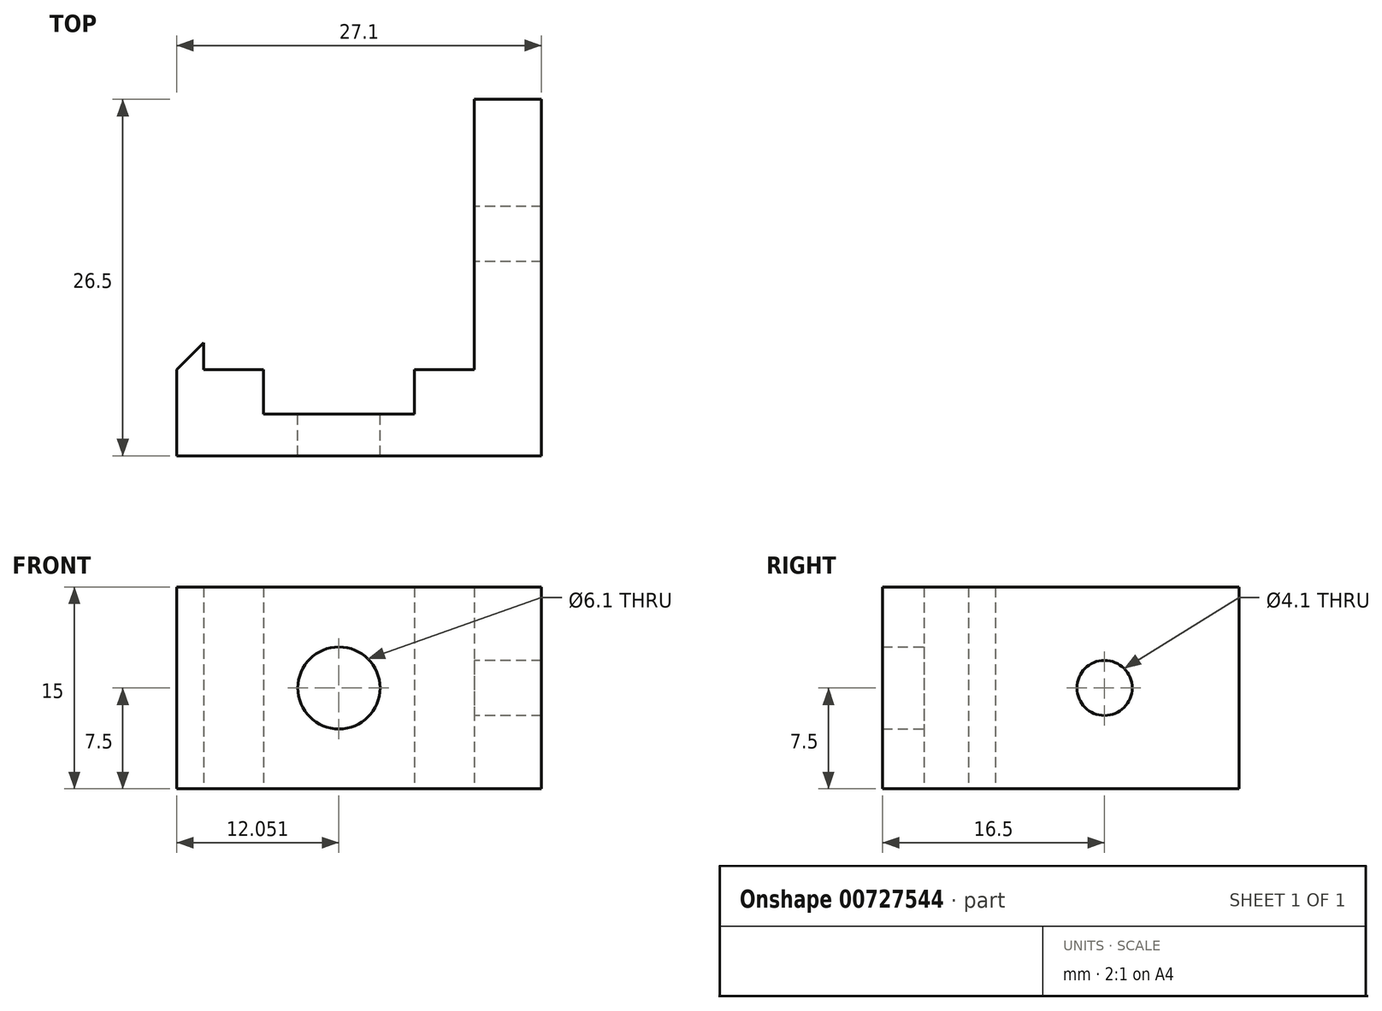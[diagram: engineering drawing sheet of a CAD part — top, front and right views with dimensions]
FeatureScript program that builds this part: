
annotation { "Feature Type Name" : "Feature", "Feature Type Description" : "" }
export const myFeature = defineFeature(function(context is Context, id is Id, definition is map)
    precondition{}
    {
        {
            var Q0;
            Q0=qCreatedBy(makeId("Top.planeOp"),FACE);
            var sketch = newSketch(context, id + "F0", { "sketchPlane" : qUnion([Q0])});
            skLineSegment(sketch, "E0", {"start": v(-8.68, -5.1) * mm, "end": v(-8.68, -7.1) * mm});
            skLineSegment(sketch, "E1", {"start": v(-8.68, -7.1) * mm, "end": v(-4.23, -7.1) * mm});
            skLineSegment(sketch, "E2", {"start": v(-4.23, -7.1) * mm, "end": v(-4.23, -10.4) * mm});
            skLineSegment(sketch, "E3", {"start": v(-4.23, -10.4) * mm, "end": v(6.97, -10.4) * mm});
            skLineSegment(sketch, "E4", {"start": v(6.97, -10.4) * mm, "end": v(6.97, -7.1) * mm});
            skLineSegment(sketch, "E5", {"start": v(6.97, -7.1) * mm, "end": v(11.42, -7.1) * mm});
            skLineSegment(sketch, "E6", {"start": v(11.42, 13) * mm, "end": v(16.42, 13) * mm});
            skLineSegment(sketch, "E7", {"start": v(16.42, 13) * mm, "end": v(16.42, -13.5) * mm});
            skLineSegment(sketch, "E8", {"start": v(16.42, -13.5) * mm, "end": v(-10.68, -13.5) * mm});
            skLineSegment(sketch, "E9", {"start": v(11.42, -7.1) * mm, "end": v(11.42, 13) * mm});
            skLineSegment(sketch, "E10", {"start": v(-8.68, -5.1) * mm, "end": v(-10.68, -7.1) * mm});
            skLineSegment(sketch, "E11", {"start": v(-10.68, -7.1) * mm, "end": v(-10.68, -13.5) * mm});
            skSolve(sketch);
        }
        {
            var Q0;
            Q0=makeQuery(id+"F0.imprint","IMPRINT",FACE,{"disambiguationData":[TD([[makeQuery(id+"F0.imprint","IMPRINT",EDGE,{"derivedFrom":sQuery(id+"F0.wireOp",EDGE,"E0")}),-1.0]])]});
            extrude(context, id + "F1", {"entities" : qUnion([Q0]), "depth" : 15 * mm, "offsetDistance" : 25 * mm});
        }
        {
            var Q0;
            Q0=makeQuery(id+"F1.opExtrude","SWEPT_FACE",FACE,{"disambiguationData":[OSD([sQuery(id+"F0.wireOp",EDGE,"E8")])]});
            var sketch = newSketch(context, id + "F2", { "sketchPlane" : qUnion([Q0])});
            skLineSegment(sketch, "E12", {"start": v(-4.23, 15) * mm, "end": v(6.97, 0) * mm, "construction": true});
            skPoint(sketch, "E13", {"position": v(1.37, 7.5) * mm});
            skLineSegment(sketch, "E14.0.0", {"start": v(6.97, 0) * mm, "end": v(-4.23, 0) * mm});
            skLineSegment(sketch, "E14.0.1", {"start": v(-4.23, 0) * mm, "end": v(-4.23, 15) * mm});
            skLineSegment(sketch, "E14.0.2", {"start": v(-4.23, 15) * mm, "end": v(6.97, 15) * mm});
            skLineSegment(sketch, "E14.0.3", {"start": v(6.97, 15) * mm, "end": v(6.97, 0) * mm});
            skSolve(sketch);
        }
        {
            var Q0;
            Q0=makeQuery(id+"F1.opExtrude","SWEPT_FACE",FACE,{"disambiguationData":[OSD([sQuery(id+"F0.wireOp",EDGE,"E7")])]});
            var sketch = newSketch(context, id + "F3", { "sketchPlane" : qUnion([Q0])});
            skLineSegment(sketch, "E15", {"start": v(13, 7.5) * mm, "end": v(-13.5, 7.5) * mm, "construction": true});
            skPoint(sketch, "E16", {"position": v(3, 7.5) * mm});
            skSolve(sketch);
        }
        {
            var Q0;
            Q0=sQuery(id+"F3.wireOp",VERTEX,"E16");
            var Q1;
            Q1=makeQuery(id+"F1.opExtrude","SWEPT_BODY",BODY,{"disambiguationData":[OSD([sQuery(id+"F0.wireOp",EDGE,"tfD9IGne-o31S-FscQ-8mek-Q3zjmK2Im2si"),sQuery(id+"F0.wireOp",EDGE,"FHpSC8xo-NXI9-o9hM-GA0Q-vl3GxMdGdn2Q"),sQuery(id+"F0.wireOp",EDGE,"y6kVXhI1-hwev-n2a0-pJKP-5HNpy6AnlQlM"),sQuery(id+"F0.wireOp",EDGE,"LtyYGiiP-rCPs-9tJH-mjaD-8RSchmz6TQnb"),sQuery(id+"F0.wireOp",EDGE,"E0"),sQuery(id+"F0.wireOp",EDGE,"E1"),sQuery(id+"F0.wireOp",EDGE,"E2"),sQuery(id+"F0.wireOp",EDGE,"E3"),sQuery(id+"F0.wireOp",EDGE,"E4"),sQuery(id+"F0.wireOp",EDGE,"E5"),sQuery(id+"F0.wireOp",EDGE,"E6"),sQuery(id+"F0.wireOp",EDGE,"E7"),sQuery(id+"F0.wireOp",EDGE,"E8"),sQuery(id+"F0.wireOp",EDGE,"E9"),sQuery(id+"F0.wireOp",EDGE,"4zuwiMRx-Zabb-Sv2b-a6I2-T9s16QXHJLWN")])]});
            hole(context, id + "F4", {"style" : HoleStyle.SIMPLE, "endStyle" : HoleEndStyle.BLIND, "holeDiameter" : 4.1 * mm, "majorDiameter" : 20 * mm, "holeDepth" : 7 * mm, "tappedDepth" : 30 * mm, "tapClearance" : 3, "startFromSketch" : true, "locations" : qUnion([Q0]), "scope" : qUnion([Q1])});
        }
        {
            var Q0;
            Q0=sQuery(id+"F2.wireOp",VERTEX,"E13");
            var Q1;
            Q1=makeQuery(id+"F1.opExtrude","SWEPT_BODY",BODY,{"disambiguationData":[OSD([sQuery(id+"F0.wireOp",EDGE,"tfD9IGne-o31S-FscQ-8mek-Q3zjmK2Im2si"),sQuery(id+"F0.wireOp",EDGE,"FHpSC8xo-NXI9-o9hM-GA0Q-vl3GxMdGdn2Q"),sQuery(id+"F0.wireOp",EDGE,"y6kVXhI1-hwev-n2a0-pJKP-5HNpy6AnlQlM"),sQuery(id+"F0.wireOp",EDGE,"LtyYGiiP-rCPs-9tJH-mjaD-8RSchmz6TQnb"),sQuery(id+"F0.wireOp",EDGE,"E0"),sQuery(id+"F0.wireOp",EDGE,"E1"),sQuery(id+"F0.wireOp",EDGE,"E2"),sQuery(id+"F0.wireOp",EDGE,"E3"),sQuery(id+"F0.wireOp",EDGE,"E4"),sQuery(id+"F0.wireOp",EDGE,"E5"),sQuery(id+"F0.wireOp",EDGE,"E6"),sQuery(id+"F0.wireOp",EDGE,"E7"),sQuery(id+"F0.wireOp",EDGE,"E8"),sQuery(id+"F0.wireOp",EDGE,"E9"),sQuery(id+"F0.wireOp",EDGE,"4zuwiMRx-Zabb-Sv2b-a6I2-T9s16QXHJLWN")])]});
            hole(context, id + "F5", {"style" : HoleStyle.SIMPLE, "endStyle" : HoleEndStyle.BLIND, "holeDiameter" : 6.1 * mm, "majorDiameter" : 5 * mm, "holeDepth" : 7 * mm, "tappedDepth" : 30 * mm, "tapClearance" : 3, "startFromSketch" : true, "locations" : qUnion([Q0]), "scope" : qUnion([Q1])});
        }
    });
